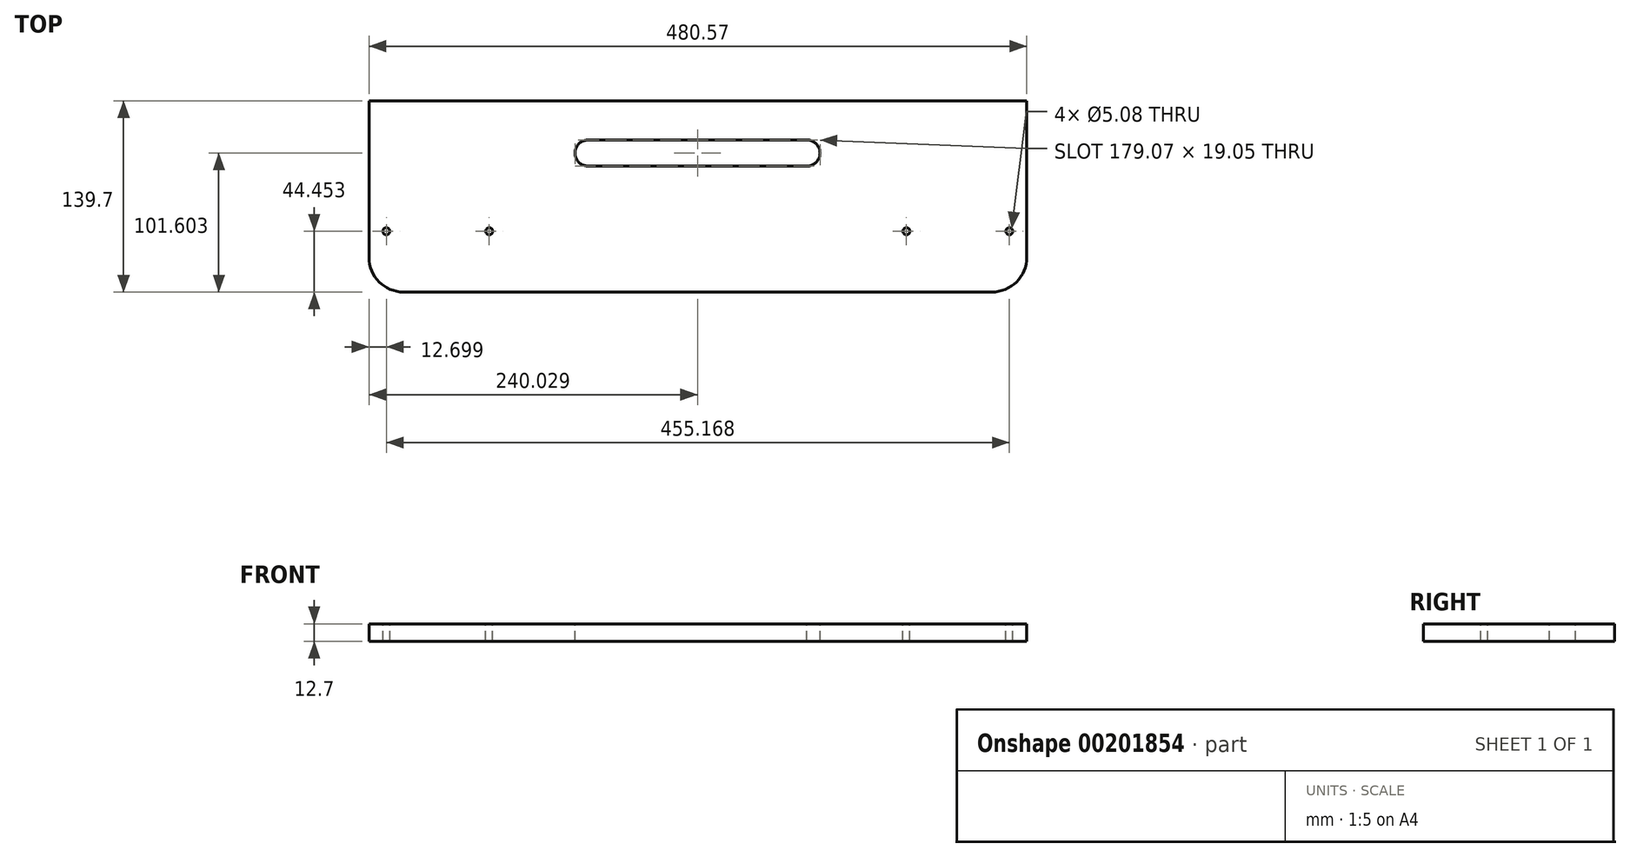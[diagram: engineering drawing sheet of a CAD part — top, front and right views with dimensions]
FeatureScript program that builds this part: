
annotation { "Feature Type Name" : "Feature", "Feature Type Description" : "" }
export const myFeature = defineFeature(function(context is Context, id is Id, definition is map)
    precondition{}
    {
        {
            var Q0;
            Q0=qCreatedBy(makeId("Top.planeOp"),FACE);
            var sketch = newSketch(context, id + "F0", { "sketchPlane" : qUnion([Q0])});
            skLineSegment(sketch, "E0.bottom", {"start": v(-47.81, -19.4) * mm, "end": v(432.76, -19.4) * mm});
            skLineSegment(sketch, "E0.top", {"start": v(-47.81, 120.3) * mm, "end": v(432.76, 120.3) * mm});
            skLineSegment(sketch, "E0.left", {"start": v(-47.81, -19.4) * mm, "end": v(-47.81, 120.3) * mm});
            skLineSegment(sketch, "E0.right", {"start": v(432.76, -19.4) * mm, "end": v(432.76, 120.3) * mm});
            skSolve(sketch);
        }
        {
            var Q0;
            Q0=makeQuery(id+"F0.imprint","IMPRINT",FACE,{"disambiguationData":[TD([[makeQuery(id+"F0.imprint","IMPRINT",EDGE,{"derivedFrom":sQuery(id+"F0.wireOp",EDGE,"E0.bottom")}),1.0]])]});
            extrude(context, id + "F1", {"entities" : qUnion([Q0]), "oppositeDirection" : true, "depth" : 12.7 * mm});
        }
        {
            var Q0;
            Q0=makeQuery(id+"F1.opExtrude","CAP_FACE",FACE,{"disambiguationData":[OSD([sQuery(id+"F0.wireOp",EDGE,"E0.bottom"),sQuery(id+"F0.wireOp",EDGE,"E0.top"),sQuery(id+"F0.wireOp",EDGE,"E0.left"),sQuery(id+"F0.wireOp",EDGE,"E0.right")])],"isStart":true});
            var sketch = newSketch(context, id + "F2", { "sketchPlane" : qUnion([Q0])});
            skCircle(sketch, "E1", {"center": v(-35.11, 25.04) * mm, "radius": 2.54 * mm});
            skArc(sketch, "E2", {"start": v(112.2, 91.72) * mm, "mid": v(102.68, 82.2) * mm, "end": v(112.2, 72.67) * mm});
            skArc(sketch, "E3", {"start": v(271.96, 72.67) * mm, "mid": v(281.75, 82.2) * mm, "end": v(271.96, 91.71) * mm});
            skLineSegment(sketch, "E4", {"start": v(271.96, 91.71) * mm, "end": v(112.2, 91.72) * mm});
            skLineSegment(sketch, "E5", {"start": v(271.96, 72.67) * mm, "end": v(112.2, 72.67) * mm});
            skCircle(sketch, "E6", {"center": v(40.07, 25.04) * mm, "radius": 2.54 * mm});
            skCircle(sketch, "E7", {"center": v(344.87, 25.04) * mm, "radius": 2.54 * mm});
            skCircle(sketch, "E8", {"center": v(420.06, 25.04) * mm, "radius": 2.54 * mm});
            skSolve(sketch);
        }
        {
            var Q0;
            Q0 = qSketchRegion(id + "F2", true);
            extrude(context, id + "F3", {"entities" : qUnion([Q0]), "operationType" : NewBodyOperationType.REMOVE, "oppositeDirection" : true, "depth" : 25.4 * mm});
        }
        {
            var Q0;
            Q0=makeQuery(id+"F1.opExtrude","SWEPT_EDGE",EDGE,{"disambiguationData":[OSD([sQuery(id+"F0.wireOp",EDGE,"E0.bottom"),sQuery(id+"F0.wireOp",EDGE,"E0.left")])]});
            var Q1;
            Q1=makeQuery(id+"F1.opExtrude","SWEPT_EDGE",EDGE,{"disambiguationData":[OSD([sQuery(id+"F0.wireOp",EDGE,"E0.bottom"),sQuery(id+"F0.wireOp",EDGE,"E0.right")])]});
            fillet(context, id + "F4", {"entities" : qUnion([Q0, Q1]), "radius" : 25.4 * mm, "tangentPropagation" : true, "allowEdgeOverflow" : false});
        }
    });
